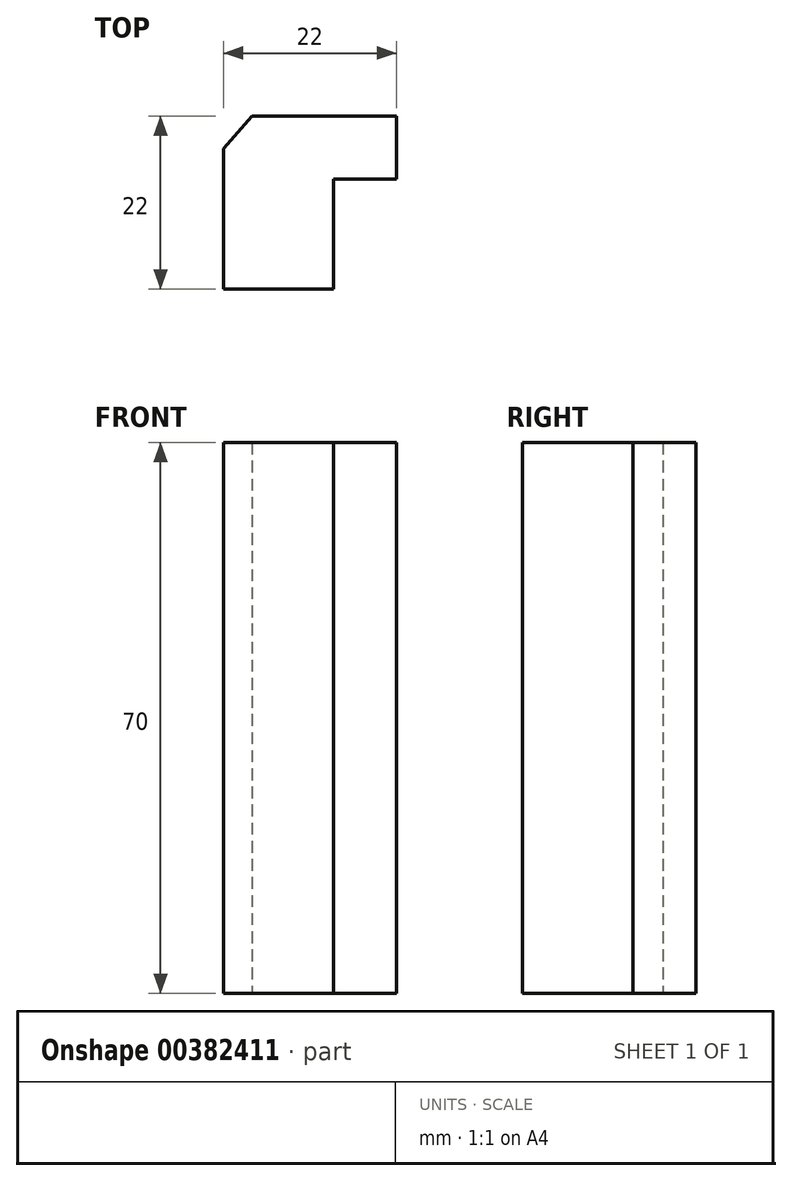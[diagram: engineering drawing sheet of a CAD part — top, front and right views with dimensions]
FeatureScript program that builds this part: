
annotation { "Feature Type Name" : "Feature", "Feature Type Description" : "" }
export const myFeature = defineFeature(function(context is Context, id is Id, definition is map)
    precondition{}
    {
        {
            var Q0;
            Q0=qCreatedBy(makeId("Top.planeOp"),FACE);
            var sketch = newSketch(context, id + "F0", { "sketchPlane" : qUnion([Q0])});
            skLineSegment(sketch, "E0", {"start": v(0, 0) * mm, "end": v(0, 17.84) * mm});
            skLineSegment(sketch, "E1", {"start": v(0, 17.84) * mm, "end": v(3.65, 22) * mm});
            skLineSegment(sketch, "E2", {"start": v(3.65, 22) * mm, "end": v(22, 22) * mm});
            skLineSegment(sketch, "E3", {"start": v(22, 22) * mm, "end": v(22, 14) * mm});
            skLineSegment(sketch, "E4", {"start": v(22, 14) * mm, "end": v(14, 14) * mm});
            skLineSegment(sketch, "E5", {"start": v(14, 14) * mm, "end": v(14, 0) * mm});
            skLineSegment(sketch, "E6", {"start": v(14, 0) * mm, "end": v(0, 0) * mm});
            skSolve(sketch);
        }
        {
            var Q0;
            Q0=makeQuery(id+"F0.imprint","IMPRINT",FACE,{"disambiguationData":[TD([[makeQuery(id+"F0.imprint","IMPRINT",EDGE,{"derivedFrom":sQuery(id+"F0.wireOp",EDGE,"E0")}),-1.0]])]});
            extrude(context, id + "F1", {"entities" : qUnion([Q0]), "depth" : 70 * mm});
        }
    });
